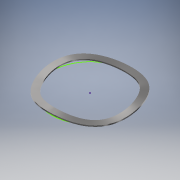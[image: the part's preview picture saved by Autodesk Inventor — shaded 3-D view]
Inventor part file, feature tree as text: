
AUTODESK INVENTOR PART (.ipt)
format: ipt  version: 2018 (Build 220112000, 112)  size: 220,672 bytes
history: native  units: mm (DEFAULTED — no unit token found)
features: sketch x9, other x2, loft x1
ambient origin geometry x8: Origin, YZ Plane, XZ Plane, XY Plane, X Axis, Y Axis, Z Axis, Center Point
bodies: Solid1 (feature_tree)
feature tree (12):
  other  "WP60"
  other  "WP120"
  sketch  "Sketch1"  dims[d0=60.0deg d1=120.0deg d5=0.7mm]
  loft  "Loft7"
  sketch  "Sketch9"  dims[d13=4.0mm d14=42.0mm d15=3.0mm d16=0.7mm d17=4.0mm d18=42.0mm d19=0.7mm d20=4.0mm d21=42.0mm d22=3.0mm d117=0.0mm d118=90.0deg d119=0.0mm d120=90.0deg d121=0.0mm d122=90.0deg d123=0.0mm d124=90.0deg d125=0.0mm d126=90.0deg d127=0.0mm d128=90.0deg d129=0.0mm d130=90.0deg]
  sketch  "Sketch2"  dims[d6=4.0mm]
  sketch  "Sketch3"  dims[d7=42.0mm]
  sketch  "Sketch4"  dims[d9=0.7mm]
  sketch  "Sketch5"  dims[d10=4.0mm]
  sketch  "Sketch6"  dims[d11=42.0mm]
  sketch  "Sketch8"  dims[d12=0.7mm]
  sketch  "3D Sketch2"
